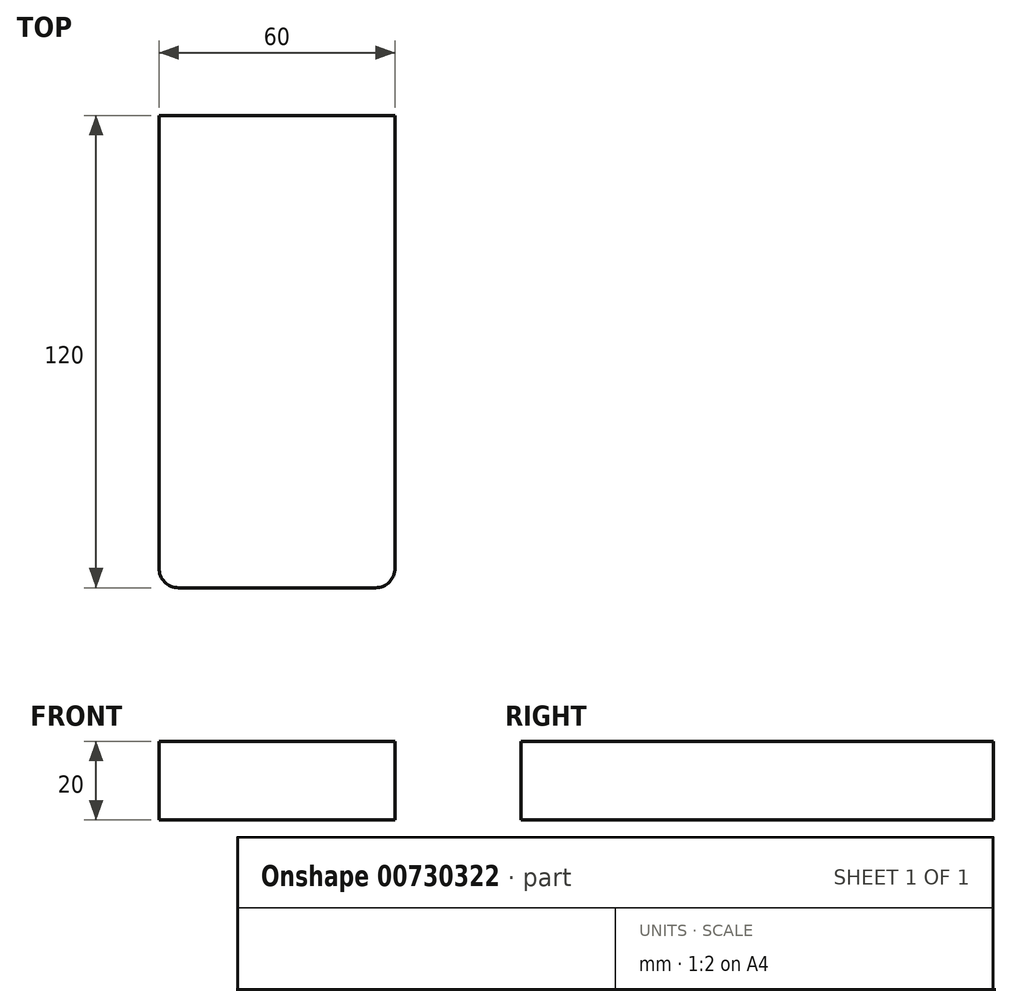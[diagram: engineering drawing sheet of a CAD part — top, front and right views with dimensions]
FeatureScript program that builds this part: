
annotation { "Feature Type Name" : "Feature", "Feature Type Description" : "" }
export const myFeature = defineFeature(function(context is Context, id is Id, definition is map)
    precondition{}
    {
        {
            var Q0;
            Q0=qCreatedBy(makeId("Top.planeOp"),FACE);
            var sketch = newSketch(context, id + "F0", { "sketchPlane" : qUnion([Q0])});
            skLineSegment(sketch, "E0.bottom", {"start": v(30, -60) * mm, "end": v(-30, -60) * mm});
            skLineSegment(sketch, "E0.top", {"start": v(30, 60) * mm, "end": v(-30, 60) * mm});
            skLineSegment(sketch, "E0.left", {"start": v(30, -60) * mm, "end": v(30, 60) * mm});
            skLineSegment(sketch, "E0.right", {"start": v(-30, -60) * mm, "end": v(-30, 60) * mm});
            skPoint(sketch, "E0.middle", {"position": v(0, 0) * mm});
            skSolve(sketch);
        }
        {
            var Q0;
            Q0=makeQuery(id+"F0.imprint","IMPRINT",FACE,{"disambiguationData":[TD([[makeQuery(id+"F0.imprint","IMPRINT",EDGE,{"derivedFrom":sQuery(id+"F0.wireOp",EDGE,"E0.bottom")}),-1.0]])]});
            extrude(context, id + "F1", {"entities" : qUnion([Q0]), "depth" : 20 * mm, "offsetDistance" : 25 * mm});
        }
        {
            var Q0;
            Q0=makeQuery(id+"F1.opExtrude","SWEPT_EDGE",EDGE,{"disambiguationData":[OSD([sQuery(id+"F0.wireOp",EDGE,"E0.bottom"),sQuery(id+"F0.wireOp",EDGE,"E0.left")])]});
            var Q1;
            Q1=makeQuery(id+"F1.opExtrude","SWEPT_EDGE",EDGE,{"disambiguationData":[OSD([sQuery(id+"F0.wireOp",EDGE,"E0.bottom"),sQuery(id+"F0.wireOp",EDGE,"E0.right")])]});
            fillet(context, id + "F2", {"entities" : qUnion([Q0, Q1]), "radius" : 5 * mm, "tangentPropagation" : true, "allowEdgeOverflow" : false});
        }
    });
